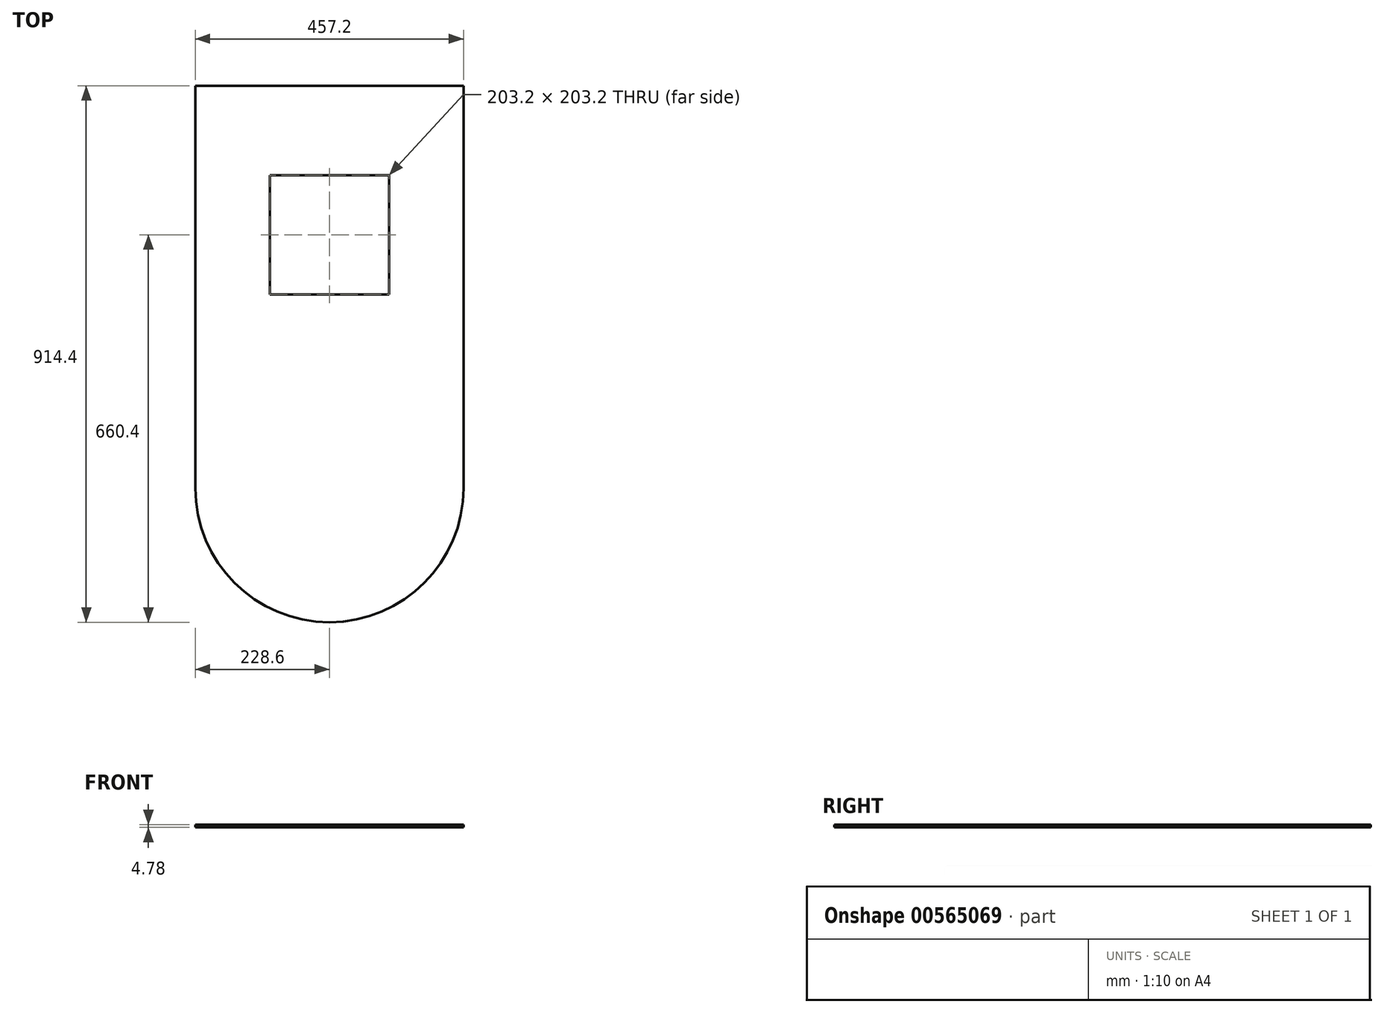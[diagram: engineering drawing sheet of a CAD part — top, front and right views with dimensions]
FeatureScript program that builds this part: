
annotation { "Feature Type Name" : "Feature", "Feature Type Description" : "" }
export const myFeature = defineFeature(function(context is Context, id is Id, definition is map)
    precondition{}
    {
        {
            var Q0;
            Q0=qCreatedBy(makeId("Top.planeOp"),FACE);
            var sketch = newSketch(context, id + "F0", { "sketchPlane" : qUnion([Q0])});
            skLineSegment(sketch, "E0.bottom", {"start": v(228.6, 0) * mm, "end": v(-228.6, 0) * mm});
            skLineSegment(sketch, "E0.top", {"start": v(228.6, 914.4) * mm, "end": v(-228.6, 914.4) * mm});
            skLineSegment(sketch, "E0.left", {"start": v(228.6, 0) * mm, "end": v(228.6, 914.4) * mm});
            skLineSegment(sketch, "E0.right", {"start": v(-228.6, 0) * mm, "end": v(-228.6, 914.4) * mm});
            skPoint(sketch, "E0.middle", {"position": v(0, 457.2) * mm});
            skSolve(sketch);
        }
        {
            var Q0;
            Q0=makeQuery(id+"F0.imprint","IMPRINT",FACE,{"disambiguationData":[TD([[makeQuery(id+"F0.imprint","IMPRINT",EDGE,{"derivedFrom":sQuery(id+"F0.wireOp",EDGE,"E0.bottom")}),-1.0]])]});
            extrude(context, id + "F1", {"entities" : qUnion([Q0]), "depth" : 4.78 * mm, "offsetDistance" : 25.4 * mm});
        }
        {
            var Q0;
            Q0=makeQuery(id+"F1.opExtrude","SWEPT_EDGE",EDGE,{"disambiguationData":[OSD([sQuery(id+"F0.wireOp",EDGE,"E0.bottom"),sQuery(id+"F0.wireOp",EDGE,"E0.left")])]});
            var Q1;
            Q1=makeQuery(id+"F1.opExtrude","SWEPT_EDGE",EDGE,{"disambiguationData":[OSD([sQuery(id+"F0.wireOp",EDGE,"E0.bottom"),sQuery(id+"F0.wireOp",EDGE,"E0.right")])]});
            fillet(context, id + "F2", {"entities" : qUnion([Q0, Q1]), "radius" : 228.6 * mm, "tangentPropagation" : true, "allowEdgeOverflow" : false});
        }
        {
            var Q0;
            Q0=makeQuery(id+"F1.opExtrude","CAP_FACE",FACE,{"disambiguationData":[OSD([sQuery(id+"F0.wireOp",EDGE,"E0.bottom"),sQuery(id+"F0.wireOp",EDGE,"E0.top"),sQuery(id+"F0.wireOp",EDGE,"E0.left"),sQuery(id+"F0.wireOp",EDGE,"E0.right")])],"isStart":false});
            var sketch = newSketch(context, id + "F3", { "sketchPlane" : qUnion([Q0])});
            skLineSegment(sketch, "E1.bottom", {"start": v(101.6, 762) * mm, "end": v(-101.6, 762) * mm});
            skLineSegment(sketch, "E1.top", {"start": v(101.6, 558.8) * mm, "end": v(-101.6, 558.8) * mm});
            skLineSegment(sketch, "E1.left", {"start": v(101.6, 762) * mm, "end": v(101.6, 558.8) * mm});
            skLineSegment(sketch, "E1.right", {"start": v(-101.6, 762) * mm, "end": v(-101.6, 558.8) * mm});
            skPoint(sketch, "E1.middle", {"position": v(0, 660.4) * mm});
            skSolve(sketch);
        }
        {
            var Q0;
            Q0=makeQuery(id+"F3.imprint","IMPRINT",FACE,{"disambiguationData":[TD([[makeQuery(id+"F3.imprint","IMPRINT",EDGE,{"derivedFrom":sQuery(id+"F3.wireOp",EDGE,"E1.bottom")}),-1.0]])]});
            extrude(context, id + "F4", {"entities" : qUnion([Q0]), "operationType" : NewBodyOperationType.INTERSECT, "oppositeDirection" : true, "depth" : 25.4 * mm, "offsetDistance" : 25.4 * mm});
        }
        {
            var Q0;
            Q0=makeQuery(id+"F1.opExtrude","CAP_FACE",FACE,{"disambiguationData":[OSD([sQuery(id+"F0.wireOp",EDGE,"E0.bottom"),sQuery(id+"F0.wireOp",EDGE,"E0.top"),sQuery(id+"F0.wireOp",EDGE,"E0.left"),sQuery(id+"F0.wireOp",EDGE,"E0.right")])],"isStart":false});
            var sketch = newSketch(context, id + "F5", { "sketchPlane" : qUnion([Q0])});
            skLineSegment(sketch, "E2", {"start": v(156.48, 914.4) * mm, "end": v(156.48, 228.6) * mm});
            skSolve(sketch);
        }
    });
